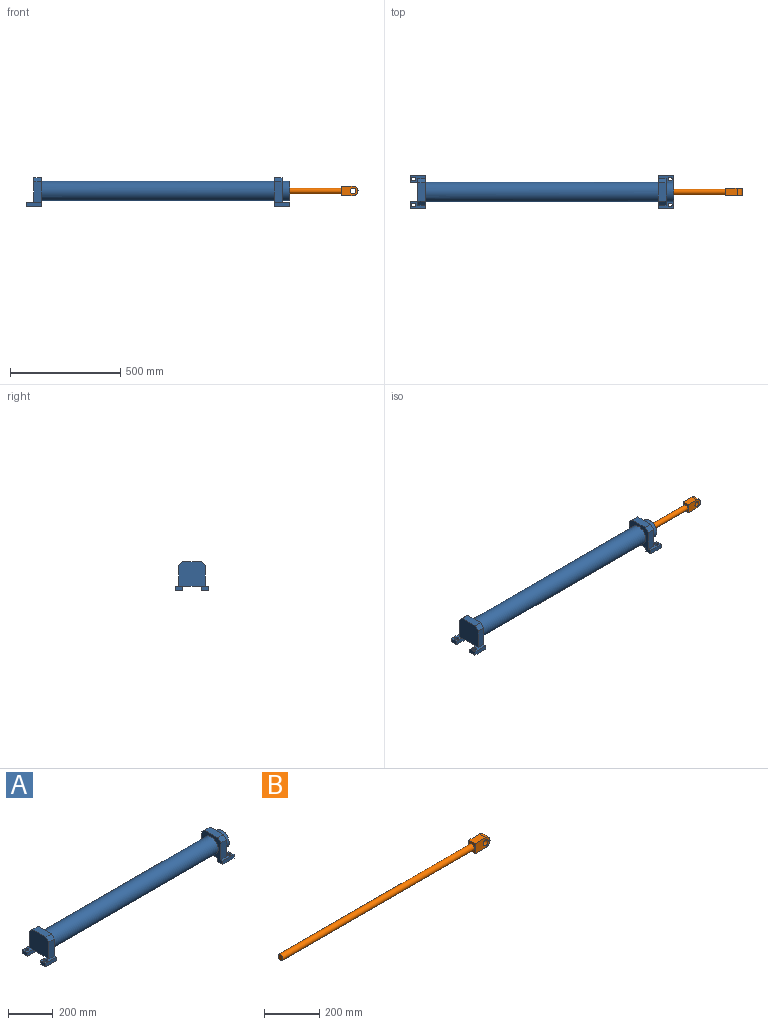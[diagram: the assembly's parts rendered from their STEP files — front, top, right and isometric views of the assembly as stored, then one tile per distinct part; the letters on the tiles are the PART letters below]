
ASSEMBLY  parts=2 mates=1
PART A: 43 faces, bbox 1193.8x149.4x130 mm
  f0: plane 85.85x34.93mm, normal (0,0,-1), area 2998.4mm2, adj f2,f4,f8,f14
  f1: plane 91.95x34.93mm, normal (0,-1,0), area 3211.3mm2, adj f2,f4,f6,f18
  f2: plane 149.35x130.05mm, normal (1,0,0), area 8031.5mm2, adj f0,f1,f3,f5,f6,f7,f8,f10
  f3: plane 91.95x34.93mm, normal (0,1,0), area 3211.3mm2, adj f2,f4,f7,f12
  f4: plane 120.65x111mm, normal (-1,0,0), area 13029mm2, adj f0,f1,f3,f5,f6,f7,f12,f18
  f5: plane 82.55x34.93mm, normal (0,0,1), area 2883.1mm2, adj f2,f4,f6,f7
  f6: plane 34.93x19.05mm, normal (0,-0.71,0.71), area 940.9mm2, adj f1,f2,f4,f5
  f7: plane 34.93x19.05mm, normal (0,0.71,0.71), area 940.9mm2, adj f2,f3,f4,f5
  f8: plane 69.85x19.05mm, normal (0,-1,0), area 1330.6mm2, adj f0,f2,f9,f12,f13
  f9: plane 31.75x19.05mm, normal (-1,0,0), area 604.8mm2, adj f8,f10,f12,f13
  f10: plane 69.85x19.05mm, normal (0,1,0), area 1330.6mm2, adj f2,f9,f12,f13
  f11: cylinder r=8.76mm len=19.05mm, axis (0,0,-1), area 1048.9mm2, adj f12,f13
  f12: plane 69.85x31.75mm, normal (0,0,1), area 1368.8mm2, adj f2,f3,f4,f8,f9,f10,f11
  f13: plane 69.85x31.75mm, normal (0,0,-1), area 1976.5mm2, adj f2,f8,f9,f10,f11
  f14: plane 69.85x19.05mm, normal (0,1,0), area 1330.6mm2, adj f0,f2,f15,f18,f19
  f15: plane 31.75x19.05mm, normal (-1,0,0), area 604.8mm2, adj f14,f16,f18,f19
  f16: plane 69.85x19.05mm, normal (0,-1,0), area 1330.6mm2, adj f2,f15,f18,f19
  f17: cylinder r=8.76mm len=19.05mm, axis (0,0,-1), area 1048.9mm2, adj f18,f19
  f18: plane 69.85x31.75mm, normal (0,0,1), area 1368.8mm2, adj f1,f2,f4,f14,f15,f16,f17
  f19: plane 69.85x31.75mm, normal (0,0,-1), area 1976.5mm2, adj f2,f14,f15,f16,f17
  f20: cylinder r=44.45mm len=1054.1mm, axis (1,0,0), area 294397mm2, adj f2,f23
  f21: plane 85.85x34.93mm, normal (0,0,-1), area 2998.4mm2, adj f23,f25,f29,f35
  f22: plane 91.95x34.93mm, normal (0,-1,0), area 3211.3mm2, adj f23,f25,f27,f39
  f23: plane 149.35x130.05mm, normal (-1,0,0), area 8031.5mm2, adj f20,f21,f22,f24,f26,f27,f28,f29
  f24: plane 91.95x34.93mm, normal (0,1,0), area 3211.3mm2, adj f23,f25,f28,f33
  f25: plane 120.65x111mm, normal (1,0,0), area 6821.8mm2, adj f21,f22,f24,f26,f27,f28,f33,f39
  f26: plane 82.55x34.93mm, normal (0,0,1), area 2883.1mm2, adj f23,f25,f27,f28
  f27: plane 34.93x19.05mm, normal (0,-0.71,0.71), area 940.9mm2, adj f22,f23,f25,f26
  f28: plane 34.93x19.05mm, normal (0,0.71,0.71), area 940.9mm2, adj f23,f24,f25,f26
  f29: plane 69.85x19.05mm, normal (0,-1,0), area 1330.6mm2, adj f21,f23,f30,f33,f34
  f30: plane 31.75x19.05mm, normal (1,0,0), area 604.8mm2, adj f29,f31,f33,f34
  f31: plane 69.85x19.05mm, normal (0,1,0), area 1330.6mm2, adj f23,f30,f33,f34
  f32: cylinder r=8.76mm len=19.05mm, axis (0,0,-1), area 1048.9mm2, adj f33,f34
  f33: plane 69.85x31.75mm, normal (0,0,1), area 1368.8mm2, adj f23,f24,f25,f29,f30,f31,f32
  f34: plane 69.85x31.75mm, normal (0,0,-1), area 1976.5mm2, adj f23,f29,f30,f31,f32
  f35: plane 69.85x19.05mm, normal (0,1,0), area 1330.6mm2, adj f21,f23,f36,f39,f40
  f36: plane 31.75x19.05mm, normal (1,0,0), area 604.8mm2, adj f35,f37,f39,f40
  f37: plane 69.85x19.05mm, normal (0,-1,0), area 1330.6mm2, adj f23,f36,f39,f40
  f38: cylinder r=8.76mm len=19.05mm, axis (0,0,-1), area 1048.9mm2, adj f39,f40
  f39: plane 69.85x31.75mm, normal (0,0,1), area 1368.8mm2, adj f22,f23,f25,f35,f36,f37,f38
  f40: plane 69.85x31.75mm, normal (0,0,-1), area 1976.5mm2, adj f23,f35,f36,f37,f38
  f41: plane 88.9x88.9mm, normal (1,0,0), area 6207.2mm2, adj f42
  f42: cylinder r=44.45mm len=88.9mm, axis (1,0,0), area 9754.1mm2, adj f25,f41
PART B: 9 faces, bbox 1054.1x31.8x44.5 mm
  f0: plane 76.2x44.45mm, normal (0,-1,0), area 2668.4mm2, adj f1,f3,f4,f7,f8
  f1: plane 53.98x31.75mm, normal (0,0,-1), area 1713.7mm2, adj f0,f2,f4,f7
  f2: plane 76.2x44.45mm, normal (0,1,0), area 2668.4mm2, adj f1,f3,f4,f7,f8
  f3: plane 53.98x31.75mm, normal (0,0,1), area 1713.7mm2, adj f0,f2,f4,f7
  f4: plane 44.45x31.75mm, normal (-1,0,0), area 904.6mm2, adj f0,f1,f2,f3,f5
  f5: cylinder r=12.7mm len=977.9mm, axis (1,0,0), area 78033mm2, adj f4,f6
  f6: plane 25.4x25.4mm, normal (-1,0,0), area 506.7mm2, adj f5
  f7: cylinder r=22.23mm len=44.45mm, axis (0,1,0), area 2216.8mm2, adj f0,f1,f2,f3
  f8: cylinder r=12.7mm len=31.75mm, axis (0,-1,0), area 2533.5mm2, adj f0,f2
PLACE A t=(45.66,-184.29,-430.49)mm fixed
PLACE B t=(239.97,-184.29,-430.49)mm
MATE slider B.f5 <-> A.f20  axis (1,0,0) through (386.02,-184.29,-360.64)mm
